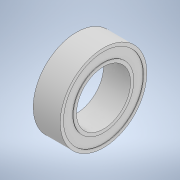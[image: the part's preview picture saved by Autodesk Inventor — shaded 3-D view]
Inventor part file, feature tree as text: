
AUTODESK INVENTOR PART (.ipt)
format: ipt  version: 2020 (Build 240168000, 168)  size: 130,560 bytes
history: native  units: mm
features: extrude x2, other x1, sketch x1
ambient origin geometry x8: Origin, YZ Plane, XZ Plane, XY Plane, X Axis, Y Axis, Z Axis, Center Point
bodies: Body1 (feature_tree)
feature tree (4):
  other  "Твердое тело1"
  sketch  "Эскиз1"
  extrude  "Выдавливание1"  Depth=5.0mm
  extrude  "Выдавливание2"  Depth=8.0mm
